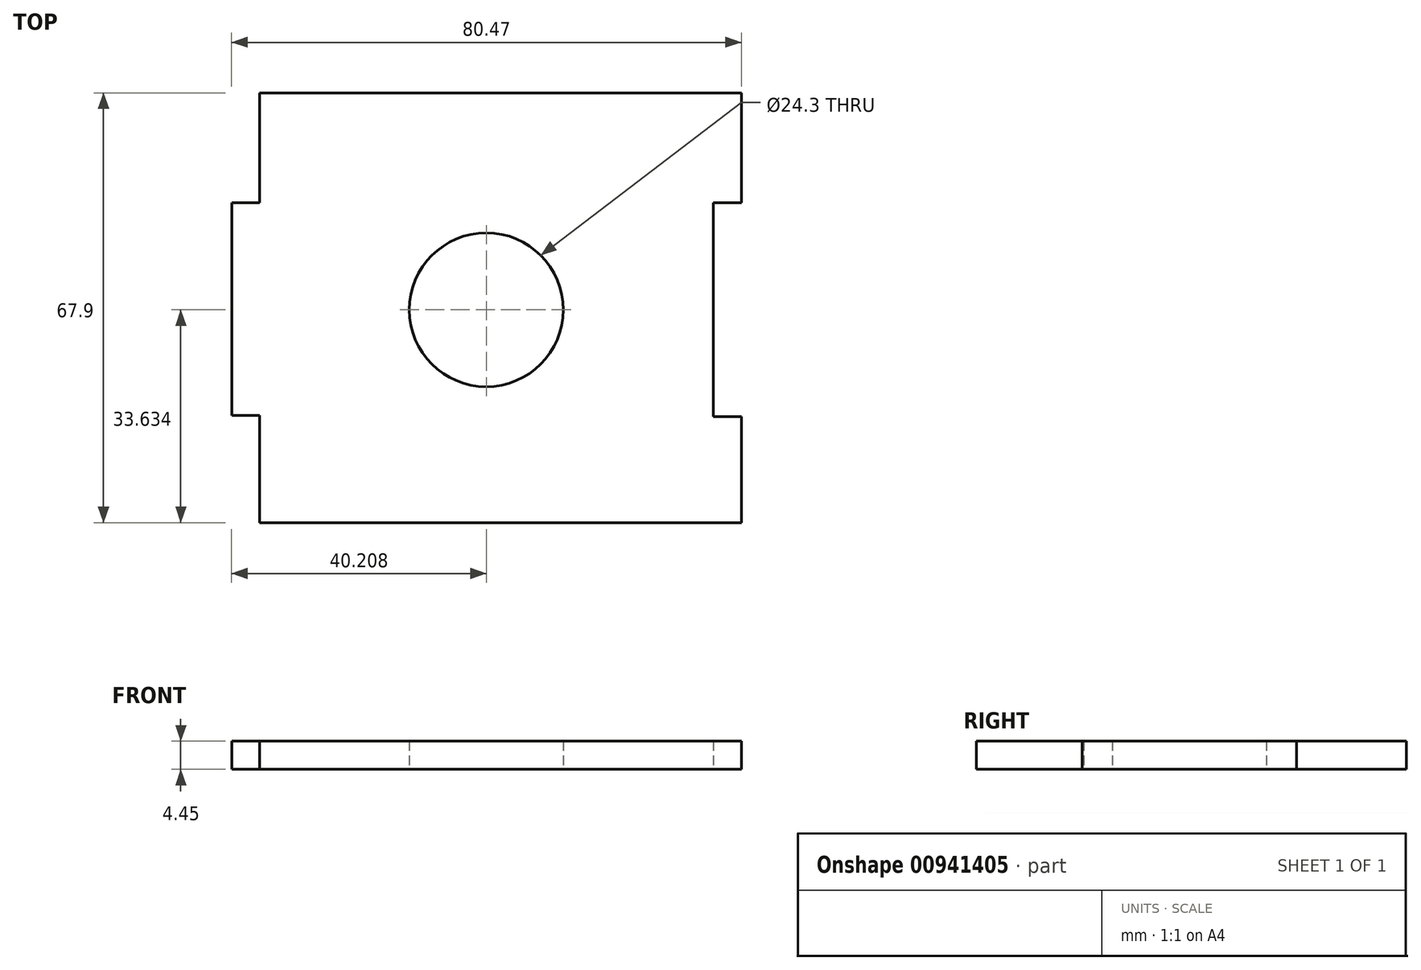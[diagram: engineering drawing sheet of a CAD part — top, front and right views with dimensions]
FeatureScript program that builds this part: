
annotation { "Feature Type Name" : "Feature", "Feature Type Description" : "" }
export const myFeature = defineFeature(function(context is Context, id is Id, definition is map)
    precondition{}
    {
        {
            var Q0;
            Q0=qCreatedBy(makeId("Top.planeOp"),FACE);
            var sketch = newSketch(context, id + "F0", { "sketchPlane" : qUnion([Q0])});
            skLineSegment(sketch, "E0.bottom", {"start": v(-50.59, 20.39) * mm, "end": v(-45.93, 20.39) * mm});
            skLineSegment(sketch, "E0.top", {"start": v(-50.59, -13.2) * mm, "end": v(-45.93, -13.2) * mm});
            skLineSegment(sketch, "E0.left", {"start": v(-50.59, 20.39) * mm, "end": v(-50.59, -13.2) * mm});
            skLineSegment(sketch, "E1.bottom", {"start": v(-46.2, 37.75) * mm, "end": v(25.43, 37.75) * mm});
            skLineSegment(sketch, "E1.top", {"start": v(-46.2, -30.15) * mm, "end": v(25.43, -30.15) * mm});
            skLineSegment(sketch, "E1.left", {"start": v(-46.2, 37.75) * mm, "end": v(-46.2, 20.39) * mm});
            skLineSegment(sketch, "E1.right", {"start": v(25.43, 20.39) * mm, "end": v(25.43, -13.42) * mm});
            skLineSegment(sketch, "E2.bottom", {"start": v(25.43, 20.39) * mm, "end": v(29.88, 20.39) * mm});
            skLineSegment(sketch, "E2.top", {"start": v(25.43, 37.75) * mm, "end": v(29.88, 37.75) * mm});
            skLineSegment(sketch, "E2.right", {"start": v(29.88, 20.39) * mm, "end": v(29.88, 37.75) * mm});
            skLineSegment(sketch, "E3.MirrorCS", {"start": v(25.43, -13.42) * mm, "end": v(29.88, -13.42) * mm});
            skLineSegment(sketch, "E4.MirrorCS", {"start": v(29.88, -13.42) * mm, "end": v(29.88, -30.15) * mm});
            skLineSegment(sketch, "E5", {"start": v(25.43, -30.15) * mm, "end": v(29.88, -30.15) * mm});
            skPoint(sketch, "E6.MirrorCS.end.orphan", {"position": v(29.88, -30.78) * mm});
            skPoint(sketch, "E6.MirrorCS.start.orphan", {"position": v(25.43, -30.78) * mm});
            skLineSegment(sketch, "E7.trimOffspring", {"start": v(-46.2, -13.2) * mm, "end": v(-46.2, -30.15) * mm});
            skCircle(sketch, "E8", {"center": v(-10.38, 3.48) * mm, "radius": 12.15 * mm});
            skPoint(sketch, "E8.centerSnap0", {"position": v(-10.38, 37.75) * mm});
            skSolve(sketch);
        }
        {
            var Q0;
            {var subQ1=sQuery(id+"F0.wireOp",EDGE,"E0.left");Q0=makeQuery(id+"F0.imprint","IMPRINT",FACE,{"disambiguationData":[TD([[makeQuery(id+"F0.imprint","IMPRINT",EDGE,{"derivedFrom":subQ1}),1.0]])]});}
            extrude(context, id + "F1", {"entities" : qUnion([Q0]), "depth" : 4.45 * mm, "offsetDistance" : 25 * mm});
        }
    });
